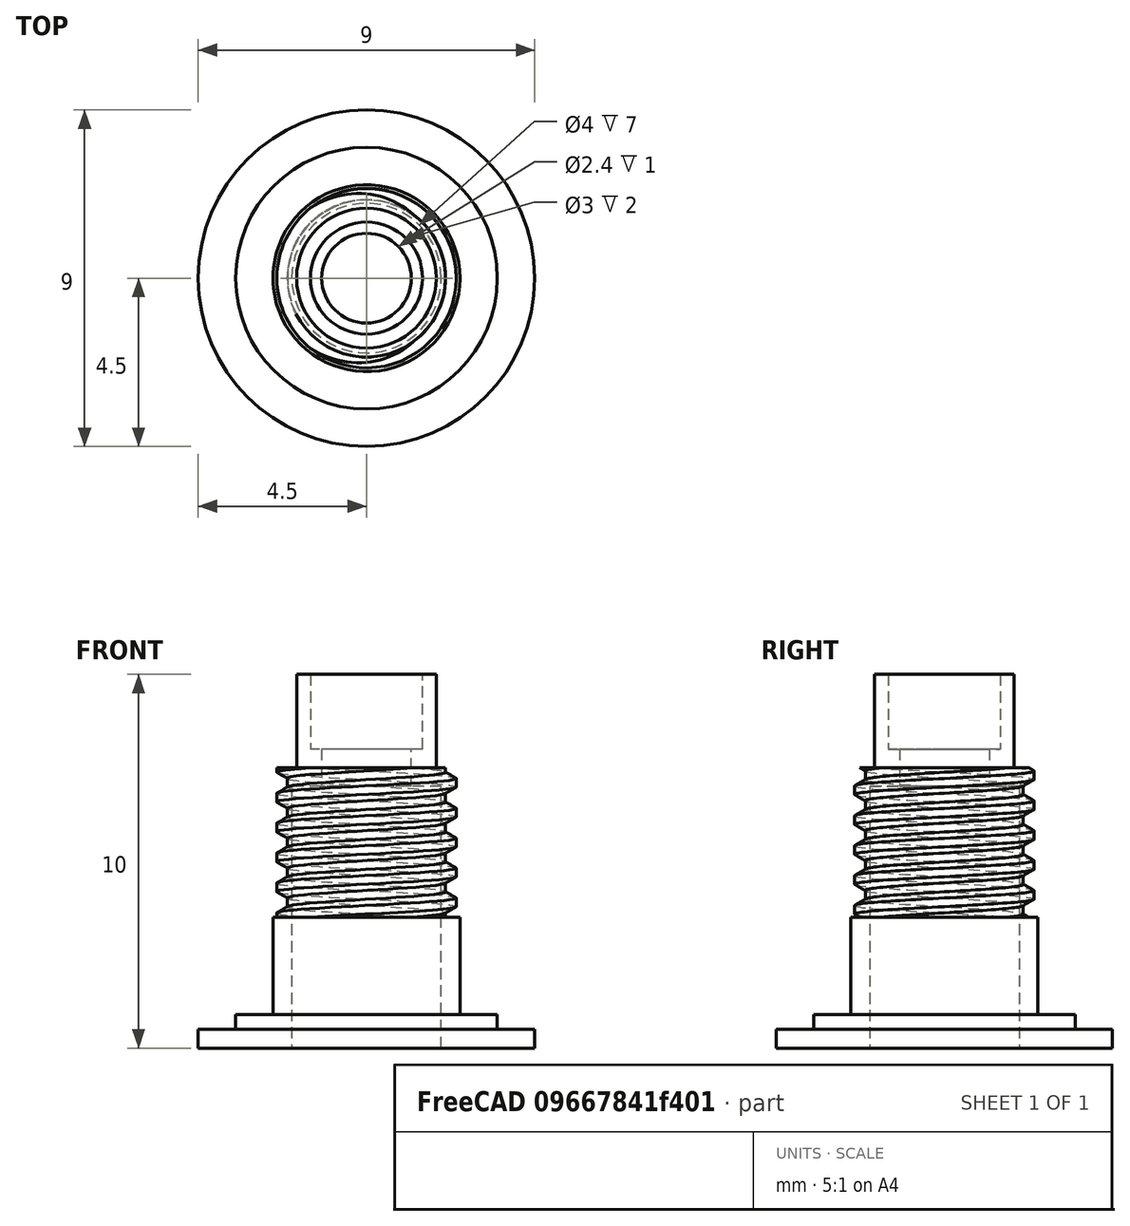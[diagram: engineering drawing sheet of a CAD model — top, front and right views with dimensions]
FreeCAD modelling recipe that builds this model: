
FCSTD DOCUMENT  (FreeCAD 0.20R)
Label: XL30FinalAppertureHolder
License: All rights reserved
LicenseURL: http://en.wikipedia.org/wiki/All_rights_reserved
objects: Part::Cylinder×8, Part::MultiFuse×2, Part::Cut×2, PartDesign::AdditiveCylinder×1, PartDesign::Hole×1, PartDesign::Body×1, Part::Feature×1
note: 18 computed .brp shape members not serialized (recipe doc carries the construction recipe); baked Part::Feature solids carry a one-line shape summary decoded from their .brp

FEATURE [Part::Cylinder] Cylinder  label="Zylinder"
  Angle = 360
  AttacherType = Attacher::AttachEngine3D
  FirstAngle = 0
  Height = 0.5
  Radius = 4.5
  SecondAngle = 0
FEATURE [Part::Cylinder] Cylinder001  label="Zylinder001"
  Angle = 360
  AttacherType = Attacher::AttachEngine3D
  FirstAngle = 0
  Height = 0.9
  Radius = 3.5
  SecondAngle = 0
FEATURE [Part::Cylinder] Cylinder002  label="Zylinder002"
  Angle = 360
  AttacherType = Attacher::AttachEngine3D
  FirstAngle = 0
  Height = 3.5
  Radius = 2.5
  SecondAngle = 0
FEATURE [Part::Cylinder] Cylinder003  label="Zylinder003"
  Angle = 360
  AttacherType = Attacher::AttachEngine3D
  FirstAngle = 0
  Height = 4
  Placement = pos=(0,0,3.5) rot=(0,0,1;0rad)
  Radius = 2.4
  SecondAngle = 0
FEATURE [Part::Cylinder] Cylinder004  label="Zylinder004"
  Angle = 360
  AttacherType = Attacher::AttachEngine3D
  FirstAngle = 0
  Height = 10
  Radius = 1.87
  SecondAngle = 0
FEATURE [Part::MultiFuse] Fusion
  Shapes = -> [Cylinder004,Cylinder,Cylinder001,Cylinder002,Cylinder003]
FEATURE [Part::Cylinder] Cylinder005  label="Zylinder005"
  Angle = 360
  AttacherType = Attacher::AttachEngine3D
  FirstAngle = 0
  Height = 100
  Radius = 1.2
  SecondAngle = 0
FEATURE [Part::Cylinder] Cylinder006  label="Zylinder006"
  Angle = 360
  AttacherType = Attacher::AttachEngine3D
  FirstAngle = 0
  Height = 7
  Radius = 2
  SecondAngle = 0
FEATURE [Part::Cylinder] Cylinder007  label="Zylinder007"
  Angle = 360
  AttacherType = Attacher::AttachEngine3D
  FirstAngle = 0
  Height = 10
  Placement = pos=(0,0,8) rot=(0,0,1;0rad)
  Radius = 1.5
  SecondAngle = 0
FEATURE [Part::MultiFuse] Fusion001
  Shapes = -> [Cylinder007,Cylinder005,Cylinder006]
FEATURE [Part::Cut] Cut
  Base = -> Fusion
  Tool = -> Fusion001
FEATURE [PartDesign::AdditiveCylinder] Cylinder008
  Angle = 360
  AttacherType = Attacher::AttachEngine3D
  FirstAngle = 0
  Height = 4
  Radius = 3
  SecondAngle = 0
FEATURE [PartDesign::Hole] Hole
  BaseFeature = -> Cylinder008
  CustomThreadClearance = 0
  Depth = 18.9163
  DepthType = 0
  Diameter = 4.224
  DrillForDepth = false
  DrillPoint = 1
  DrillPointAngle = 118
  HoleCutCountersinkAngle = 90
  HoleCutCustomValues = false
  HoleCutDepth = 0
  HoleCutDiameter = 6.1
  HoleCutType = 0
  ModelThread = true
  Profile = -> Cylinder008 [Face3]
  Tapered = false
  TaperedAngle = 90
  ThreadClass = 0
  ThreadDepth = 18.9163
  ThreadDepthType = 0
  ThreadDirection = 0
  ThreadFit = 0
  ThreadSize = 13
  ThreadType = 1
  Threaded = true
  UseCustomThreadClearance = false
FEATURE [PartDesign::Body] Body  label="ThreadCutterM3"
  Group = -> [Cylinder008,Hole]
  Origin = -> Origin
  Placement = pos=(0,0,3.5) rot=(0,0,1;0rad)
  Tip = -> Hole
FEATURE [Part::Cut] Cut001
  Base = -> Cut
  Tool = -> Body
FEATURE [Part::Feature] Cut001_solid  label="XL30FinalAppertureHolder"
  shape: bbox 9 x 9 x 10 mm, 44 faces (baked)
